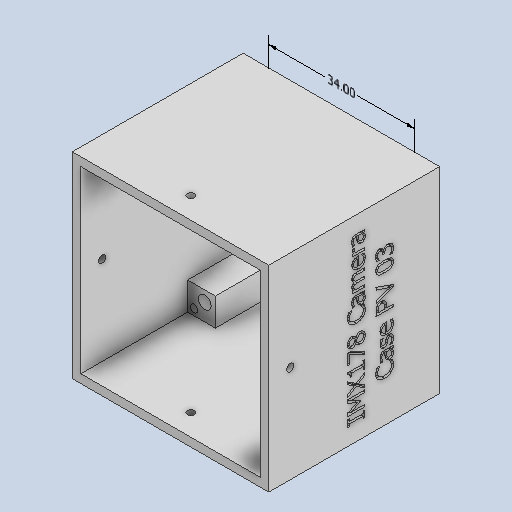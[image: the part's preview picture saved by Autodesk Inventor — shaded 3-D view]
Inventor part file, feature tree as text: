
AUTODESK INVENTOR PART (.ipt)
format: ipt  version: 2022.1 (Build 261234000, 234)  size: 876,032 bytes
history: native  units: mm
features: sketch x6, other x5, hole x3, reference x3, extrude x2, emboss x1
ambient origin geometry x8: Origin, YZ Plane, XZ Plane, XY Plane, X Axis, Y Axis, Z Axis, Center Point
bodies: Solid5 (feature_tree)
feature tree (20):
  other  "Annotations"
  extrude  "Extrusion9"  Depth=34.0mm
  extrude  "Extrusion10"  Depth=42.0mm
  emboss  "Emboss2"
  hole  "Hole1"  [1 undecoded]
  hole  "Hole2"  [1 undecoded]
  hole  "Hole3"  [1 undecoded]
  sketch  "Sketch8"  dims[d46=34.0mm d47=34.0mm]
  sketch  "Sketch9"  dims[d48=3.0mm d49=42.0mm]
  sketch  "Sketch10"  dims[d50=42.0mm d51=2.0mm]
  sketch  "Sketch11"  dims[d52=2.0mm d53=29.0mm]
  sketch  "Sketch12"  dims[d54=29.0mm d55=15.0mm d56=0.0mm]
  reference  "Reference1"
  reference  "Reference2"
  sketch  "Sketch13"  dims[d57=25.0mm d58=0.0mm d59=1.0mm d60=0.0mm d61=39.0mm d62=39.0mm d63=1.69418mm d64=4.369mm d65=3.023mm d66=2.0mm d67=14.3117mm d68=8.0mm d69=20.594885mm d70=1.69418mm d71=4.369mm d72=4.369mm d73=2.0mm d74=14.3117mm d75=8.0mm d76=20.594885mm d77=1.69418mm d78=4.369mm d79=4.0mm d80=2.0mm d81=90.0deg d82=8.0mm d83=20.594885mm d86=34.0mm]
  reference  "Reference3"
  parser-record x1  (decoder bookkeeping rows leaked as tree rows — omitted from the tree; the rows remain in map.json)
  other  "IMX178 Camera Case Assembly.iam"
  other  "IMX178 Camera Case Cap:1"
  other  "Linear Dimension 1"
note: 3 required parameter values undecoded (feature->parameter linkage not recoverable at this tier; creation-order binding heuristic only, values carry confidence <= 0.55)
note: 1 file-system path scrubbed to <path> (originals preserved in map.json)
